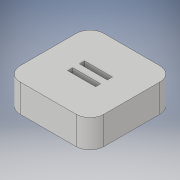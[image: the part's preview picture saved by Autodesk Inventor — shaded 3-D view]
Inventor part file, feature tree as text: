
AUTODESK INVENTOR PART (.ipt)
format: ipt  version: 2019 (Build 230136000, 136)  size: 139,776 bytes
history: native  units: in
note: dims shown in document units (in); Inventor stores cm internally (conversion verified against a paired STEP export)
features: extrude x4, sketch x3, fillet x1
ambient origin geometry x8: Origin, YZ Plane, XZ Plane, XY Plane, X Axis, Y Axis, Z Axis, Center Point
bodies: Solid1 (feature_tree)
feature tree (8):
  extrude  "Extrusion1"  Depth=0.75in
  sketch  "Sketch2"  dims[d2=0.375in d3=0.375in]
  extrude  "Extrusion2"  Depth=0.375in
  extrude  "Extrusion3"  Depth=0.25in
  extrude  "Extrusion4"  Depth=0.045in
  fillet  "Fillet1"  Radius=0.125in
  sketch  "Sketch1"  dims[d0=0.75in d1=0.75in]
  sketch  "Sketch3"  dims[d4=0.25in d5=0.0in d6=0.25in d7=0.045in d8=0.125in d11=0.06in d12=0.03in d13=0.25in d14=0.045in d15=0.045in d16=0.0in d17=0.09in d18=0.0in d19=0.09in d20=0.0in d21=0.125in]
